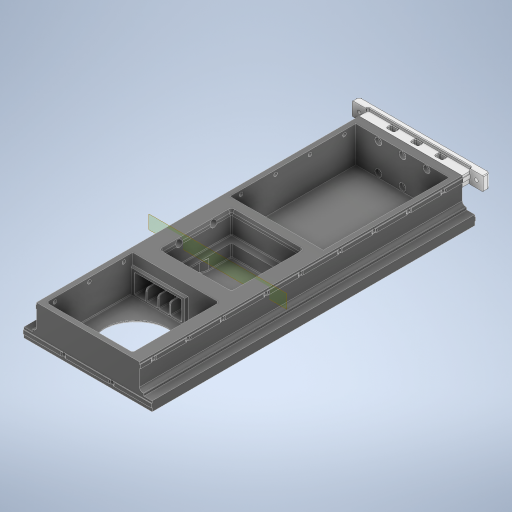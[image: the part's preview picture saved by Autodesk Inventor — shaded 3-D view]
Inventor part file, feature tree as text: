
AUTODESK INVENTOR PART (.ipt)
format: ipt  version: 2024 (Build 280153000, 153)  size: 1,913,856 bytes
history: native  units: mm
features: projected_geometry x39, sketch x33, extrude x31, fillet x21, hole x10, plane x7, chamfer x6, other x4, thicken_offset x3, mirror x3
ambient origin geometry x8: Origin, YZ Plane, XZ Plane, XY Plane, X Axis, Y Axis, Z Axis, Center Point
bodies: Solid1 (feature_tree)
feature tree (157):
  sketch  "Sketch1"  dims[d0=20.0mm d1=20.0mm]
  extrude  "Extrusion1"  Depth=20.0mm
  extrude  "Extrusion2"  Depth=20.0mm
  hole  "Hole3"  [1 undecoded]
  extrude  "Extrusion8"  Depth=6.0mm
  extrude  "Extrusion9"  Depth=0.2mm
  extrude  "Extrusion13"  Depth=7.0mm
  sketch  "Sketch17"  dims[d12=4.25mm d13=7.0mm]
  extrude  "Extrusion12"  Depth=2.0mm
  extrude  "Extrusion16"  Depth=1.0mm
  extrude  "Extrusion18"  Depth=1.0mm
  extrude  "Extrusion19"  Depth=12.0mm
  chamfer  "Chamfer2"  Distance=1.0mm
  extrude  "Extrusion20"  TaperAngle=0.0deg  [1 undecoded]
  hole  "Hole6"  [1 undecoded]
  sketch  "Sketch25"  dims[d23=12.0mm d24=0.0mm d59=70.0mm]
  plane  "Work Plane2"
  extrude  "Extrusion21"  Depth=47.5mm
  sketch  "Sketch26"  dims[d60=5.4mm d61=6.0mm d62=10.0mm d63=5.0mm d64=90.0deg d65=8.0mm d66=150.0deg]
  plane  "Work Plane3"
  extrude  "Extrusion22"  Depth=120.0mm
  extrude  "Extrusion23"  TaperAngle=0.0deg  [1 undecoded]
  extrude  "Extrusion24"  Depth=7.0mm
  fillet  "Fillet13"  Radius=2.8mm
  sketch  "Sketch28"  dims[d73=6.0mm d74=0.0mm d75=0.0mm]
  thicken_offset  "Thicken1"
  thicken_offset  "Thicken2"
  thicken_offset  "Thicken3"
  extrude  "Extrusion25"  Depth=2.8mm
  extrude  "Extrusion26"  Depth=101.0mm
  extrude  "Extrusion27"  Depth=15.0mm
  fillet  "Fillet15"  Radius=9.0mm
  chamfer  "Chamfer4"  Distance=10.0mm
  fillet  "Fillet16"  Radius=27.5mm
  fillet  "Fillet17"  Radius=34.0mm
  extrude  "Extrusion28"  Depth=2.0mm
  fillet  "Fillet19"  Radius=25.0mm
  fillet  "Fillet23"  Radius=80.0mm
  fillet  "Fillet26"  Radius=80.0mm
  fillet  "Fillet27"  [1 undecoded]
  fillet  "Fillet28"  Radius=25.0mm
  fillet  "Fillet33"  Radius=20.0mm
  fillet  "Fillet34"  [1 undecoded]
  fillet  "Fillet35"  Radius=10.0mm
  fillet  "Fillet36"  [1 undecoded]
  fillet  "Fillet37"  Radius=5.0mm
  extrude  "Extrusion29"  Depth=15.0mm
  chamfer  "Chamfer5"  Distance=10.0mm
  chamfer  "Chamfer6"  Distance=30.0mm
  sketch  "Sketch36"  dims[d124=2.8mm d125=2.8mm]
  hole  "Hole7"  [1 undecoded]
  hole  "Hole8"  [1 undecoded]
  mirror  "Mirror3"
  chamfer  "Chamfer7"  Distance=17.0mm
  extrude  "Extrusion30"  Depth=17.0mm
  hole  "Hole9"  [1 undecoded]
  fillet  "Fillet38"  Radius=0.654498mm
  hole  "Hole10"  [1 undecoded]
  chamfer  "Chamfer8"  Distance=0.654498mm
  hole  "Hole11"  [1 undecoded]
  mirror  "Mirror4"
  plane  "Work Plane5"
  hole  "Hole12"  [1 undecoded]
  extrude  "Extrusion32"  Depth=12.0mm TaperAngle=0.0deg
  extrude  "Extrusion33"  Depth=12.0mm TaperAngle=0.0deg
  extrude  "Extrusion34"  Depth=2.0mm
  extrude  "Extrusion35"  Depth=2.0mm
  fillet  "Fillet40"  Radius=2.0mm
  fillet  "Fillet41"  Radius=2.0mm
  fillet  "Fillet42"  Radius=10.0mm
  hole  "Hole13"  [1 undecoded]
  extrude  "Extrusion36"  Depth=10.0mm TaperAngle=0.0deg
  plane  "Work Plane6"
  hole  "Hole14"  [1 undecoded]
  plane  "Work Plane9"
  sketch  "Sketch51"  dims[d196=4.0mm d197=45.0deg]
  extrude  "Extrusion37"  Depth=2.0mm
  extrude  "Extrusion38"  Depth=10.0mm
  fillet  "Fillet43"  Radius=2.0mm
  fillet  "Fillet44"  Radius=2.0mm
  plane  "Work Plane10"
  fillet  "Fillet45"  Radius=4.0mm
  extrude  "Extrusion39"  Depth=12.0mm
  mirror  "Mirror5"
  sketch  "Sketch2"  dims[d4=190.0mm d5=20.0mm]
  projected_geometry  "Projected Loop1"
  sketch  "Sketch10"  dims[d6=1.0mm d7=18.0mm]
  sketch  "Sketch12"  dims[d8=6.0mm d9=6.0mm]
  projected_geometry  "Projected Loop8"
  sketch  "Sketch13"  dims[d10=0.2mm d11=0.2mm]
  projected_geometry  "Projected Loop9"
  sketch  "Sketch18"  dims[d14=10.0mm d16=2.0mm]
  projected_geometry  "Projected Loop13"
  sketch  "Sketch23"  dims[d18=468.3mm d19=0.0mm d20=1.0mm]
  projected_geometry  "Projected Loop19"
  sketch  "Sketch24"  dims[d21=5.5mm d22=1.0mm]
  projected_geometry  "Projected Loop20"
  projected_geometry  "Projected Loop21"
  projected_geometry  "Projected Loop22"
  projected_geometry  "Projected Loop23"
  projected_geometry  "Projected Loop24"
  projected_geometry  "Projected Loop25"
  projected_geometry  "Projected Loop26"
  sketch  "Sketch27"  dims[d70=5.5mm d71=1.0mm d72=0.0mm]
  projected_geometry  "Projected Loop27"
  projected_geometry  "Projected Loop28"
  other  "Srf1"
  other  "Srf2"
  other  "Srf3"
  sketch  "Sketch29"  dims[d92=90.0mm d93=105.0mm]
  projected_geometry  "Projected Loop29"
  sketch  "Sketch30"  dims[d94=105.0mm d95=47.5mm]
  projected_geometry  "Projected Loop30"
  sketch  "Sketch31"  dims[d96=120.0mm d97=120.0mm]
  projected_geometry  "Projected Loop31"
  sketch  "Sketch32"  dims[d99=52.5mm d100=0.0mm d101=0.0mm]
  projected_geometry  "Projected Loop32"
  sketch  "Sketch33"  dims[d102=7.0mm d103=0.0mm d122=2.8mm d123=2.8mm]
  projected_geometry  "Projected Loop33"
  projected_geometry  "Projected Loop34"
  projected_geometry  "Projected Loop35"
  projected_geometry  "Projected Loop36"
  projected_geometry  "Projected Loop37"
  sketch  "Sketch38"  dims[d126=101.0mm d127=101.0mm]
  sketch  "Sketch39"  dims[d128=15.0mm d129=25.0mm d130=9.0mm]
  sketch  "Sketch40"  dims[d131=78.0mm]
  sketch  "Sketch41"  dims[d132=0.5mm]
  projected_geometry  "Projected Loop38"
  projected_geometry  "Projected Loop39"
  sketch  "Sketch42"  dims[d133=150.0mm d134=10.0mm d135=0.0mm d143=27.5mm d144=0.0mm d145=34.0mm d146=0.0mm]
  projected_geometry  "Projected Loop40"
  projected_geometry  "Projected Loop41"
  projected_geometry  "Projected Loop42"
  projected_geometry  "Projected Loop45"
  projected_geometry  "Projected Loop46"
  sketch  "Sketch44"  dims[d147=2.3mm d148=2.0mm d149=45.0deg d150=14.0mm d156=25.0mm d157=0.0mm]
  projected_geometry  "Projected Loop47"
  other  "Rear Extrusion Bracket"
  sketch  "Sketch45"  dims[d163=4.4mm d164=6.0mm d165=4.0mm d166=2.0mm d167=90.0deg d168=8.0mm d169=150.0deg d170=80.0mm d171=80.0mm d172=-32.0mm d173=25.0mm d174=0.0mm d175=20.0mm d176=150.0deg d177=10.0mm d178=135.0deg d179=5.0mm]
  sketch  "Sketch46"  dims[d180=5.0mm d182=15.0mm]
  sketch  "Sketch47"  dims[d183=40.0mm]
  projected_geometry  "Projected Loop48"
  projected_geometry  "Projected Loop49"
  sketch  "Sketch48"  dims[d184=-2.0mm d185=10.0mm d186=0.0mm]
  sketch  "Sketch49"  dims[d187=2.0mm d188=30.0mm d189=0.0mm]
  projected_geometry  "Projected Loop50"
  sketch  "Sketch50"  dims[d191=12.0mm d194=30.0mm d195=0.0mm]
  projected_geometry  "Projected Loop51"
  plane  "Work Plane8"
  sketch  "Sketch52"  dims[d198=34.0mm d199=17.0mm d200=17.0mm d201=15.0deg d202=0.654498mm d203=0.654498mm d205=0.654498mm d206=15.0mm d207=19.0mm d208=0.0mm d209=19.0mm d210=0.0mm d211=19.0mm d212=0.0mm d213=2.0mm d214=2.0mm d215=2.0mm d216=2.0mm d217=10.0mm d218=0.0mm d219=10.0mm d220=0.0mm d221=10.0mm d222=0.0mm d223=2.0mm d224=6.0mm d225=2.0mm d226=3.490659mm d227=10.0mm d228=2.0mm d229=2.0mm d230=0.0mm d232=4.0mm d239=4.0mm d246=1.0mm d247=1.0mm d248=0.5mm d249=1.0mm d250=1.0mm d255=1.0mm d256=3.0mm d257=2.0mm d258=1.0mm d259=1.0mm d260=125.0mm d261=10.0mm d262=13.482833mm d263=13.482833mm d264=3.0mm d265=0.0mm d266=3.0mm d267=2.0mm d268=3.490659mm d281=4.0mm d282=2.0mm d283=3.490659mm d284=100.0mm d285=50.0mm d286=150.0mm d287=50.0mm d288=5.4mm d289=6.0mm d290=4.0mm d291=2.0mm d292=90.0deg d293=8.0mm d294=150.0deg d295=6.0mm d296=6.0mm d297=4.0mm d298=2.0mm d299=90.0deg d300=8.0mm d301=0.0mm d302=1.0mm d303=2.0mm d304=3.490659mm d305=5.4mm d306=6.0mm d307=4.0mm d308=2.0mm d309=90.0deg d310=20.0mm d311=150.0deg d312=1.0mm d313=1.0mm d314=0.0mm d315=6.0mm d316=6.0mm d317=4.0mm d318=2.0mm d319=90.0deg d320=20.0mm d321=0.0mm d322=1.0mm d323=2.0mm d324=3.490659mm d325=9.5mm d326=6.0mm d327=4.0mm d328=2.0mm d329=90.0deg d330=8.0mm d331=0.0mm d332=-7.0mm d333=9.5mm d334=6.0mm d335=4.0mm d336=2.0mm d337=90.0deg d338=8.0mm d339=0.0mm d343=57.5mm d344=65.0mm d345=55.0mm d346=1.0mm d347=10.2mm d348=0.0mm d349=10.0mm d350=0.0mm d351=20.0mm d352=20.0mm d353=3.0mm d354=8.0mm d355=0.0mm d356=10.0mm d357=0.0mm d358=2.0mm d359=4.0mm d360=1.0mm d361=5.3mm d362=6.0mm d363=10.0mm d364=5.0mm d365=90.0deg d366=8.0mm d367=0.0mm d368=0.2mm d369=0.0mm d370=-24.0mm d371=6.0mm d372=6.0mm d373=5.3mm d374=6.0mm d375=10.0mm d376=5.0mm d377=90.0deg d378=8.0mm d379=0.0mm d381=6.5mm d382=2.5mm d383=8.25mm d384=10.0mm d385=0.0mm d386=10.0mm d387=10.0mm d388=0.0mm d389=1.0mm d390=1.0mm d391=-300.0mm d392=5.0mm d393=3.25mm d394=12.0mm d395=0.0mm d139=0.0mm d140=0.0mm d141=0.0mm d142=0.0mm d251=0.0mm d252=0.0mm d253=0.0mm d254=0.0mm]
  projected_geometry  "Projected Loop52"
  extrude  "ExtrusionSrf1"  Depth=1.0mm
  extrude  "ExtrusionSrf2"  Depth=1.0mm
  extrude  "ExtrusionSrf3"  Depth=1.0mm
  projected_geometry  "Project Cut Edges2"
  projected_geometry  "Project Cut Edges3"
  projected_geometry  "Project Cut Edges4"
note: 15 required parameter values undecoded (feature->parameter linkage not recoverable at this tier; creation-order binding heuristic only, values carry confidence <= 0.55)
